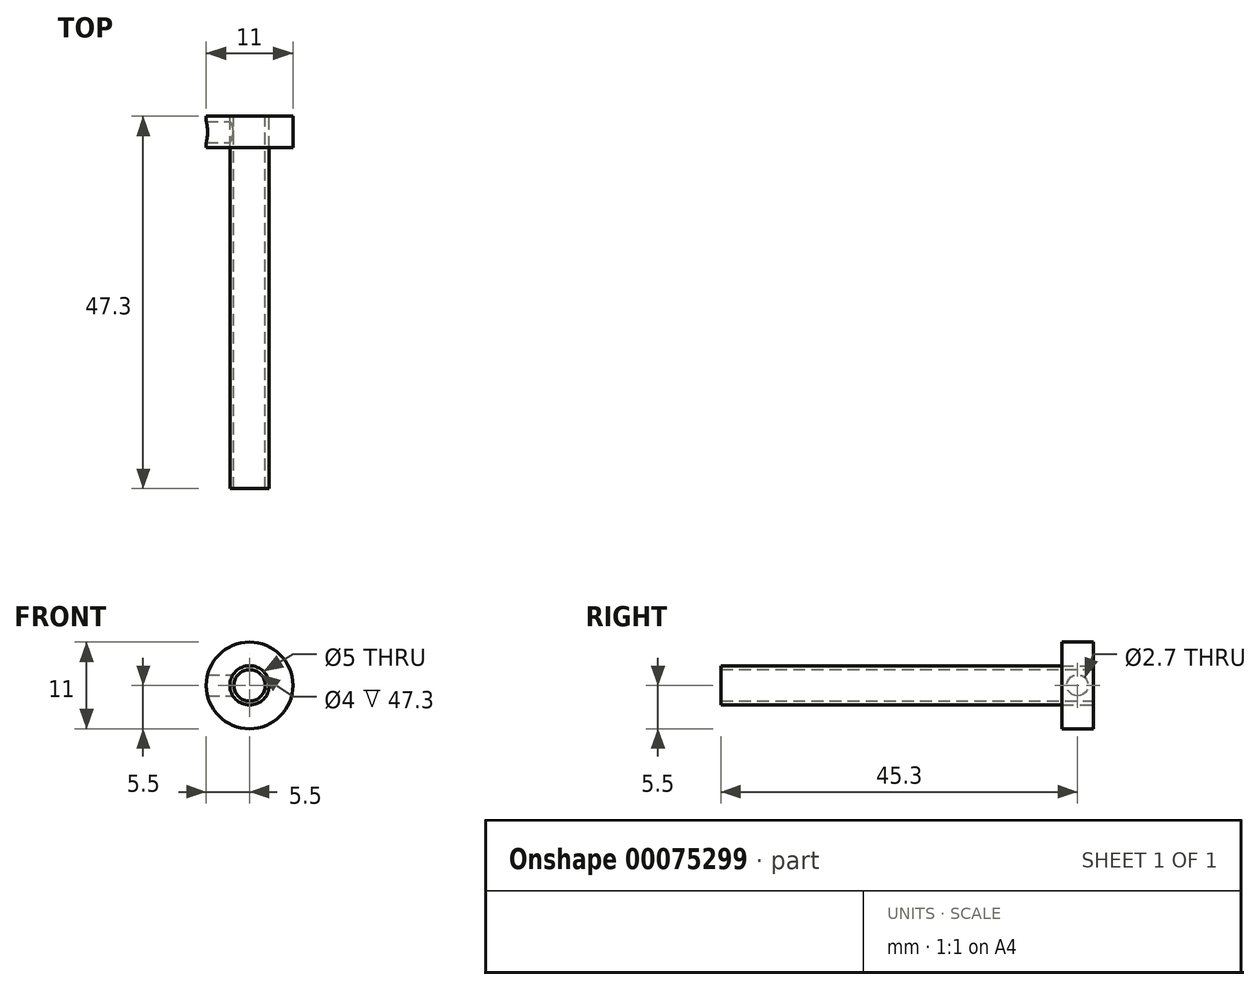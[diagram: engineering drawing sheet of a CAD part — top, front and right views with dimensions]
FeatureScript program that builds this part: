
annotation { "Feature Type Name" : "Feature", "Feature Type Description" : "" }
export const myFeature = defineFeature(function(context is Context, id is Id, definition is map)
    precondition{}
    {
        {
            var Q0;
            Q0=qCreatedBy(makeId("Front.planeOp"),FACE);
            var sketch = newSketch(context, id + "F0", { "sketchPlane" : qUnion([Q0])});
            skCircle(sketch, "E0", {"center": v(0, 0) * mm, "radius": 2 * mm});
            skCircle(sketch, "E1", {"center": v(0, 0) * mm, "radius": 2.5 * mm});
            skSolve(sketch);
        }
        {
            var Q0;
            Q0 = qSketchRegion(id + "F0", true);
            extrude(context, id + "F1", {"entities" : qUnion([Q0]), "depth" : 47.3 * mm});
        }
        {
            var Q0;
            Q0=qCreatedBy(makeId("Front.planeOp"),FACE);
            var sketch = newSketch(context, id + "F2", { "sketchPlane" : qUnion([Q0])});
            skCircle(sketch, "E2", {"center": v(0, 0) * mm, "radius": 2.5 * mm});
            skCircle(sketch, "E3", {"center": v(0, 0) * mm, "radius": 5.5 * mm});
            skSolve(sketch);
        }
        {
            var Q0;
            Q0 = qSketchRegion(id + "F2", true);
            extrude(context, id + "F3", {"entities" : qUnion([Q0]), "depth" : 4 * mm});
        }
        {
            var Q0;
            Q0=qCreatedBy(makeId("Right.planeOp"),FACE);
            var sketch = newSketch(context, id + "F4", { "sketchPlane" : qUnion([Q0])});
            skLineSegment(sketch, "E4", {"start": v(-4, 5.5) * mm, "end": v(0, 5.5) * mm, "construction": true});
            skLineSegment(sketch, "E5", {"start": v(-2, 5.5) * mm, "end": v(-2, -9.05) * mm, "construction": true});
            skCircle(sketch, "E6", {"center": v(-2, 0) * mm, "radius": 1.38 * mm});
            skSolve(sketch);
        }
        {
            var Q0;
            Q0=sQuery(id+"F4.wireOp",VERTEX,"E6.center");
            var Q1;
            Q1=makeQuery(id+"F3.opExtrude","SWEPT_BODY",BODY,{"disambiguationData":[OSD([sQuery(id+"F2.wireOp",EDGE,"E2"),sQuery(id+"F2.wireOp",EDGE,"E3")])]});
            hole(context, id + "F5", {"style" : HoleStyle.SIMPLE, "holeDiameter" : 2.7 * mm, "endStyle" : HoleEndStyle.THROUGH, "locations" : qUnion([Q0]), "scope" : qUnion([Q1])});
        }
    });
